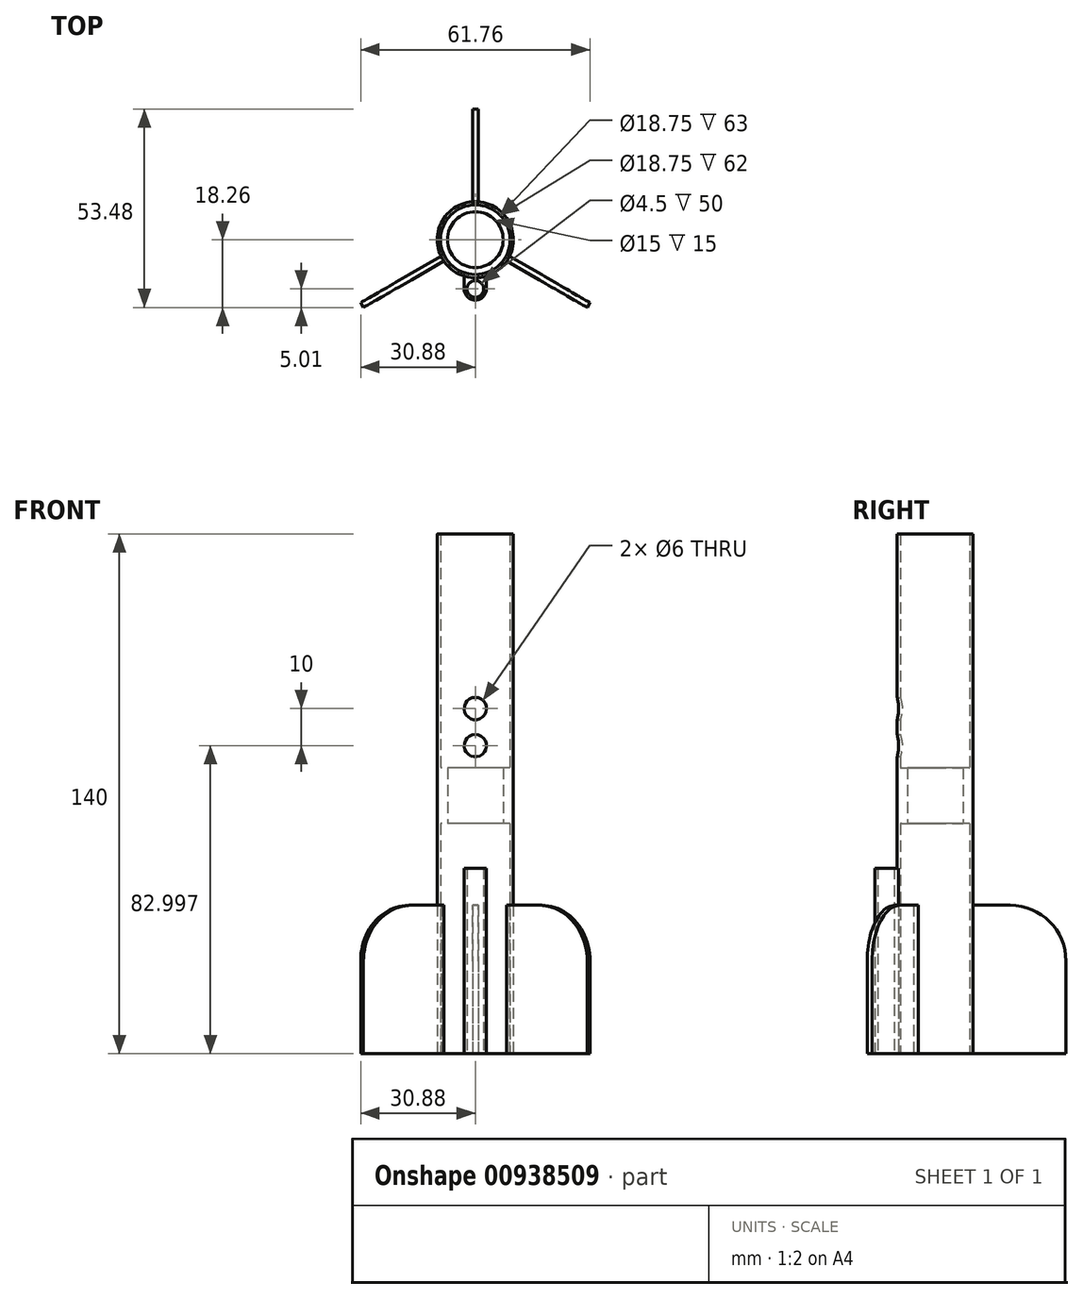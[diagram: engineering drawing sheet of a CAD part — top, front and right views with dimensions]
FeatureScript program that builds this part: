
annotation { "Feature Type Name" : "Feature", "Feature Type Description" : "" }
export const myFeature = defineFeature(function(context is Context, id is Id, definition is map)
    precondition{}
    {
        {
            var Q0;
            Q0=qCreatedBy(makeId("Top.planeOp"),FACE);
            var sketch = newSketch(context, id + "F0", { "sketchPlane" : qUnion([Q0])});
            skCircle(sketch, "E0", {"center": v(0, 0) * mm, "radius": 9.38 * mm});
            skCircle(sketch, "E1", {"center": v(0, 0) * mm, "radius": 10.25 * mm});
            skCircle(sketch, "E2", {"center": v(0, -13.25) * mm, "radius": 2.25 * mm});
            skCircle(sketch, "E3", {"center": v(0, -13.25) * mm, "radius": 3 * mm});
            skLineSegment(sketch, "E4", {"start": v(-3, -13.25) * mm, "end": v(-3, -9.8) * mm});
            skLineSegment(sketch, "E5", {"start": v(3, -13.25) * mm, "end": v(3, -9.8) * mm});
            skLineSegment(sketch, "E6.bottom", {"start": v(-0.75, 35.22) * mm, "end": v(0.75, 35.22) * mm});
            skLineSegment(sketch, "E6.top", {"start": v(-0.75, 10.22) * mm, "end": v(0.75, 10.22) * mm, "construction": true});
            skLineSegment(sketch, "E6.left", {"start": v(-0.75, 35.22) * mm, "end": v(-0.75, 10.22) * mm});
            skLineSegment(sketch, "E6.right", {"start": v(0.75, 35.22) * mm, "end": v(0.75, 10.22) * mm});
            skCircle(sketch, "E7", {"center": v(0, 0) * mm, "radius": 7.5 * mm});
            skSolve(sketch);
        }
        {
            var Q0;
            Q0=makeQuery(id+"F0.imprint","IMPRINT",FACE,{"disambiguationData":[TD([[makeQuery(id+"F0.imprint","IMPRINT",EDGE,{"derivedFrom":sQuery(id+"F0.wireOp",EDGE,"E0")}),-1.0]])]});
            extrude(context, id + "F1", {"entities" : qUnion([Q0]), "depth" : 140 * mm, "offsetDistance" : 25 * mm});
        }
        {
            var Q0;
            Q0=makeQuery(id+"F0.imprint","IMPRINT",FACE,{"disambiguationData":[TD([[makeQuery(id+"F0.imprint","IMPRINT",EDGE,{"derivedFrom":sQuery(id+"F0.wireOp",EDGE,"E6.bottom")}),-1.0]])]});
            extrude(context, id + "F2", {"entities" : qUnion([Q0]), "operationType" : NewBodyOperationType.ADD, "depth" : 40 * mm, "offsetDistance" : 25 * mm});
        }
        {
            var Q0;
            Q0=makeQuery(id+"F1.opExtrude","SWEPT_BODY",BODY,{"disambiguationData":[OSD([sQuery(id+"F0.wireOp",EDGE,"E0"),sQuery(id+"F0.wireOp",EDGE,"E1")])]});
            var Q1;
            Q1=makeQuery(id+"F1.opExtrude","CAP_EDGE",EDGE,{"disambiguationData":[OSD([sQuery(id+"F0.wireOp",EDGE,"E0")])],"isStart":false});
            circularPattern(context, id + "F3", {"entities" : qUnion([Q0]), "axis" : qUnion([Q1]), "angle" : 360 * degree, "instanceCount" : 3, "equalSpace" : true});
        }
        {
            var Q0;
            Q0=makeQuery(id+"F0.imprint","IMPRINT",FACE,{"disambiguationData":[TD([[makeQuery(id+"F0.imprint","IMPRINT",EDGE,{"derivedFrom":sQuery(id+"F0.wireOp",EDGE,"E2")}),-1.0]])]});
            var Q1;
            {var subQ0=sQuery(id+"F0.wireOp",EDGE,"E5");Q1=makeQuery(id+"F0.imprint","IMPRINT",FACE,{"disambiguationData":[TD([[makeQuery(id+"F0.imprint","IMPRINT",EDGE,{"derivedFrom":subQ0}),1.0]])]});}
            var Q2;
            {var subQ0=sQuery(id+"F0.wireOp",EDGE,"E4");Q2=makeQuery(id+"F0.imprint","IMPRINT",FACE,{"disambiguationData":[TD([[makeQuery(id+"F0.imprint","IMPRINT",EDGE,{"derivedFrom":subQ0}),-1.0]])]});}
            extrude(context, id + "F4", {"entities" : qUnion([Q0, Q1, Q2]), "operationType" : NewBodyOperationType.ADD, "depth" : 50 * mm, "offsetDistance" : 25 * mm});
        }
        {
            var Q0;
            Q0=makeQuery(id+"F0.imprint","IMPRINT",FACE,{"disambiguationData":[TD([[makeQuery(id+"F0.imprint","IMPRINT",EDGE,{"derivedFrom":sQuery(id+"F0.wireOp",EDGE,"E0")}),1.0]])]});
            extrude(context, id + "F5", {"entities" : qUnion([Q0]), "operationType" : NewBodyOperationType.ADD, "depth" : 77 * mm, "offsetDistance" : 25 * mm, "hasSecondDirection" : true, "secondDirectionOppositeDirection" : false, "secondDirectionDepth" : 62 * mm});
        }
        {
            var Q0;
            Q0=qCreatedBy(makeId("Front.planeOp"),FACE);
            var sketch = newSketch(context, id + "F6", { "sketchPlane" : qUnion([Q0])});
            skCircle(sketch, "E8", {"center": v(0, 83) * mm, "radius": 3 * mm});
            skCircle(sketch, "E9", {"center": v(0, 93) * mm, "radius": 3 * mm});
            skSolve(sketch);
        }
        {
            var Q0;
            Q0 = qSketchRegion(id + "F6", true);
            extrude(context, id + "F7", {"entities" : qUnion([Q0]), "operationType" : NewBodyOperationType.REMOVE, "depth" : 25 * mm, "offsetDistance" : 25 * mm});
        }
        {
            var Q0;
            Q0=makeQuery(id+"F2.opExtrude","CAP_EDGE",EDGE,{"disambiguationData":[OSD([sQuery(id+"F0.wireOp",EDGE,"E6.bottom")])],"isStart":false});
            var Q1;
            Q1=makeQuery(id+"F3.opPattern","COPY",EDGE,{"derivedFrom":makeQuery(id+"F2.opExtrude","CAP_EDGE",EDGE,{"disambiguationData":[OSD([sQuery(id+"F0.wireOp",EDGE,"E6.bottom")])],"isStart":false}),"instanceName":"2"});
            var Q2;
            Q2=makeQuery(id+"F3.opPattern","COPY",EDGE,{"derivedFrom":makeQuery(id+"F2.opExtrude","CAP_EDGE",EDGE,{"disambiguationData":[OSD([sQuery(id+"F0.wireOp",EDGE,"E6.bottom")])],"isStart":false}),"instanceName":"1"});
            fillet(context, id + "F8", {"entities" : qUnion([Q0, Q1, Q2]), "radius" : 15 * mm, "tangentPropagation" : true, "allowEdgeOverflow" : false});
        }
    });
